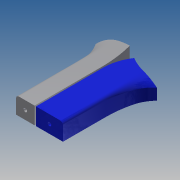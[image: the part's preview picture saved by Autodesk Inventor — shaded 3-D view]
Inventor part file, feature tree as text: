
AUTODESK INVENTOR PART (.ipt)
format: ipt  version: 2015 (Build 190159000, 159)  size: 293,376 bytes
history: native  units: mm
features: sketch x9, extrude x7, other x6, plane x2, loft x2, projected_geometry x2, fillet x1
ambient origin geometry x8: Origin, YZ Plane, XZ Plane, XY Plane, X Axis, Y Axis, Z Axis, Center Point
bodies: Body1 (feature_tree), Body2 (feature_tree), Body3 (feature_tree)
feature tree (29):
  extrude  "Extrusion2"  Depth=480.0mm
  sketch  "Skizze11"  dims[d5=700.0mm d8=480.0mm]
  extrude  "Extrusion8"  Depth=200.0mm
  sketch  "Skizze21"  dims[d9=270.0mm d10=200.0mm]
  other  "3D-Skizze3"
  plane  "Arbeitsebene10"
  loft  "Erhebung7"
  extrude  "Extrusion9"  Depth=70.0mm
  sketch  "Skizze24"  dims[d16=80.0mm d18=70.0mm]
  other  "3D-Skizze4"
  plane  "Arbeitsebene11"
  loft  "Erhebung8"
  extrude  "Extrusion10"  Depth=220.0mm
  fillet  "Rundung1"  Radius=640.0mm
  extrude  "Extrusion11"  Depth=60.0mm
  projected_geometry  "Projizierte Kontur3"
  sketch  "Skizze22"  dims[d11=170.0mm d13=120.0mm]
  other  "Fläche1"
  sketch  "Skizze23"  dims[d14=50.0mm d15=70.0mm]
  sketch  "Skizze25"  dims[d20=60.0mm d21=220.0mm d23=640.0mm]
  other  "Fläche2"
  sketch  "Skizze26"  dims[d25=60.0mm d26=60.0mm]
  sketch  "Skizze27"  dims[d27=120.0mm d28=0.0mm d69=20.0mm]
  sketch  "Skizze28"  dims[d70=20.0mm d85=30.0mm d86=30.0mm d108=10.0mm d109=0.0mm d110=50.0mm d111=50.0mm d112=80.0mm d113=400.0mm d114=0.0mm d115=50.0mm d116=50.0mm d117=0.0mm d118=90.0deg d119=0.0mm d120=90.0deg d121=0.0mm d122=90.0deg d123=0.0mm d124=90.0deg d125=400.0mm d126=0.0mm d127=50.0mm d128=50.0mm d129=80.0mm d130=400.0mm d131=0.0mm d132=50.0mm d133=50.0mm d134=0.0mm d135=90.0deg d136=0.0mm d137=90.0deg d138=0.0mm d139=90.0deg d140=0.0mm d141=90.0deg d142=400.0mm d143=0.0mm d144=10.0mm d145=25.0mm d146=100.0mm d147=0.0mm]
  projected_geometry  "Projizierte Kontur5"
  extrude  "Extrusionsfläche1"  Depth=20.0mm
  extrude  "Extrusionsfläche2"  Depth=10.0mm
  other  "3D-Schnitt1"
  other  "3D-Schnitt2"
